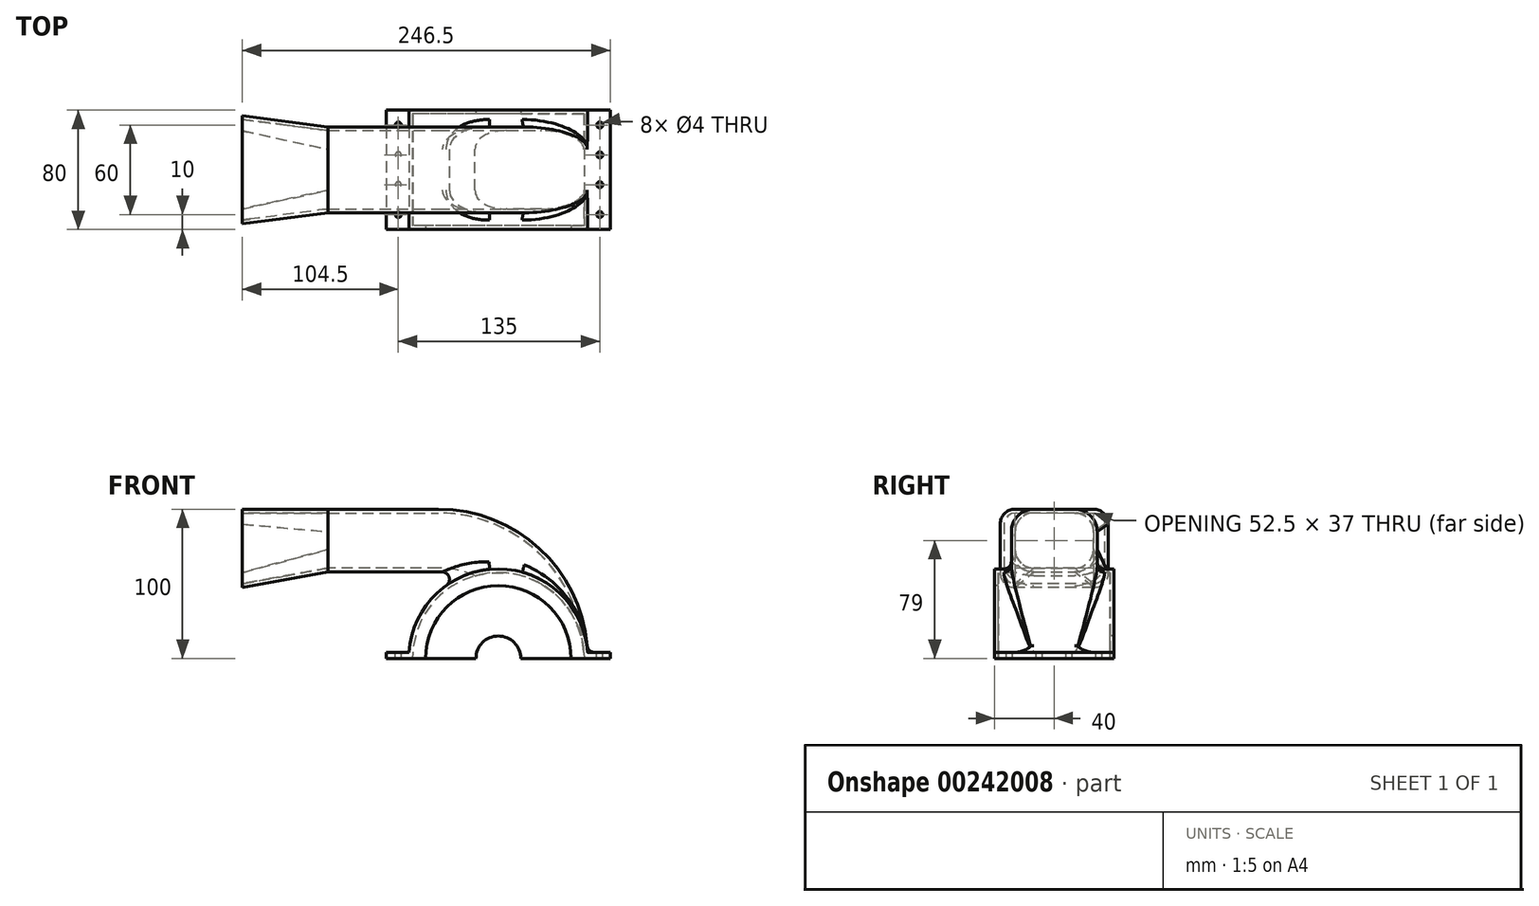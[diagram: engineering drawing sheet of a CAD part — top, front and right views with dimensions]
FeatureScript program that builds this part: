
annotation { "Feature Type Name" : "Feature", "Feature Type Description" : "" }
export const myFeature = defineFeature(function(context is Context, id is Id, definition is map)
    precondition{}
    {
        {
            var Q0;
            Q0=qCreatedBy(makeId("Front.planeOp"),FACE);
            var sketch = newSketch(context, id + "F0", { "sketchPlane" : qUnion([Q0])});
            skArc(sketch, "E0", {"start": v(15, 0) * mm, "mid": v(0, 15) * mm, "end": v(-15, 0) * mm});
            skArc(sketch, "E1", {"start": v(48.75, 0) * mm, "mid": v(0, 48.75) * mm, "end": v(-48.75, 0) * mm});
            skArc(sketch, "E2", {"start": v(59.87, 4) * mm, "mid": v(0, 60) * mm, "end": v(-59.87, 4) * mm});
            skLineSegment(sketch, "E3", {"start": v(15, 0) * mm, "end": v(75, 0) * mm});
            skLineSegment(sketch, "E4", {"start": v(-15, 0) * mm, "end": v(-75, 0) * mm});
            skLineSegment(sketch, "E5", {"start": v(75, 0) * mm, "end": v(75, 4) * mm});
            skLineSegment(sketch, "E6", {"start": v(75, 4) * mm, "end": v(59.87, 4) * mm});
            skLineSegment(sketch, "E7", {"start": v(-75, 0) * mm, "end": v(-75, 4) * mm});
            skLineSegment(sketch, "E8", {"start": v(-75, 4) * mm, "end": v(-59.87, 4) * mm});
            skPoint(sketch, "E9.orphan", {"position": v(-60, 0) * mm});
            skPoint(sketch, "E10.orphan", {"position": v(60, 0) * mm});
            skLineSegment(sketch, "E11", {"start": v(59.87, 4) * mm, "end": v(60, 0) * mm});
            skLineSegment(sketch, "E12", {"start": v(-59.87, 4) * mm, "end": v(-60, 0) * mm});
            skSolve(sketch);
        }
        {
            var Q0;
            {var subQ1=sQuery(id+"F0.wireOp",EDGE,"E1");Q0=makeQuery(id+"F0.imprint","IMPRINT",FACE,{"disambiguationData":[TD([[makeQuery(id+"F0.imprint","IMPRINT",EDGE,{"derivedFrom":subQ1}),-1.0]])]});}
            var Q1;
            {var subQ0=sQuery(id+"F0.wireOp",EDGE,"E0");Q1=makeQuery(id+"F0.imprint","IMPRINT",FACE,{"disambiguationData":[TD([[makeQuery(id+"F0.imprint","IMPRINT",EDGE,{"derivedFrom":subQ0}),-1.0]])]});}
            extrude(context, id + "F1", {"entities" : qUnion([Q0, Q1]), "oppositeDirection" : true, "depth" : 80 * mm});
        }
        {
            var Q0;
            Q0=qCreatedBy(makeId("Front.planeOp"),FACE);
            cPlane(context, id + "F2", {"entities" : qUnion([Q0]), "cplaneType" : CPlaneType.OFFSET, "offset" : 40 * mm, "oppositeDirection" : true, "width" : 150 * mm, "height" : 150 * mm});
        }
        {
            var Q0;
            Q0=qCreatedBy(id+"F2.planeOp",FACE);
            var sketch = newSketch(context, id + "F3", { "sketchPlane" : qUnion([Q0])});
            skArc(sketch, "E13.0", {"start": v(59.87, 4) * mm, "mid": v(0, 60) * mm, "end": v(-59.87, 4) * mm});
            skLineSegment(sketch, "E14", {"start": v(-114.05, 100) * mm, "end": v(-114.05, 58) * mm});
            skLineSegment(sketch, "E15", {"start": v(-114.05, 100) * mm, "end": v(-40.05, 100) * mm});
            skArc(sketch, "E16", {"start": v(-40.05, 100) * mm, "mid": v(29.23, 72.11) * mm, "end": v(59.87, 4) * mm});
            skLineSegment(sketch, "E17", {"start": v(-114.05, 58) * mm, "end": v(-15.36, 58) * mm});
            skLineSegment(sketch, "E18", {"start": v(-114.05, 100) * mm, "end": v(-171.55, 100) * mm});
            skLineSegment(sketch, "E19", {"start": v(-171.55, 100) * mm, "end": v(-171.55, 47.5) * mm});
            skLineSegment(sketch, "E20", {"start": v(-171.55, 47.5) * mm, "end": v(-114.05, 58) * mm});
            skSolve(sketch);
        }
        {
            var Q0;
            Q0=qCreatedBy(makeId("Right.planeOp"),FACE);
            cPlane(context, id + "F4", {"entities" : qUnion([Q0]), "cplaneType" : CPlaneType.OFFSET, "offset" : 114 * mm, "oppositeDirection" : true, "width" : 150 * mm, "height" : 150 * mm});
        }
        {
            var Q0;
            Q0=qCreatedBy(id+"F4.planeOp",FACE);
            var sketch = newSketch(context, id + "F5", { "sketchPlane" : qUnion([Q0])});
            skPoint(sketch, "E21", {"position": v(40, 79) * mm});
            skLineSegment(sketch, "E22.bottom", {"start": v(26.25, 100) * mm, "end": v(53.75, 100) * mm});
            skLineSegment(sketch, "E22.top", {"start": v(26.25, 58) * mm, "end": v(53.75, 58) * mm});
            skLineSegment(sketch, "E22.left", {"start": v(11.25, 85) * mm, "end": v(11.25, 73) * mm});
            skLineSegment(sketch, "E22.right", {"start": v(68.75, 85) * mm, "end": v(68.75, 73) * mm});
            skPoint(sketch, "E23.orphan", {"position": v(40, 100) * mm});
            skPoint(sketch, "E24.0.end.orphan", {"position": v(40, 58) * mm});
            skPoint(sketch, "E25.visualSharp", {"position": v(11.25, 100) * mm});
            skArc(sketch, "E25.filletArc", {"start": v(26.25, 100) * mm, "mid": v(15.64, 95.6) * mm, "end": v(11.25, 85) * mm});
            skPoint(sketch, "E26.visualSharp", {"position": v(11.25, 58) * mm});
            skArc(sketch, "E26.filletArc", {"start": v(11.25, 73) * mm, "mid": v(15.64, 62.4) * mm, "end": v(26.25, 58) * mm});
            skPoint(sketch, "E27.visualSharp", {"position": v(68.75, 58) * mm});
            skArc(sketch, "E27.filletArc", {"start": v(53.75, 58) * mm, "mid": v(64.36, 62.4) * mm, "end": v(68.75, 73) * mm});
            skPoint(sketch, "E28.visualSharp", {"position": v(68.75, 100) * mm});
            skArc(sketch, "E28.filletArc", {"start": v(68.75, 85) * mm, "mid": v(64.36, 95.6) * mm, "end": v(53.75, 100) * mm});
            skSolve(sketch);
        }
        {
            var Q0;
            Q0=makeQuery(id+"F5.imprint","IMPRINT",FACE,{"disambiguationData":[TD([[makeQuery(id+"F5.imprint","IMPRINT",EDGE,{"derivedFrom":sQuery(id+"F5.wireOp",EDGE,"E22.bottom")}),-1.0]])]});
            var Q1;
            Q1=sQuery(id+"F3.wireOp",EDGE,"E15");
            var Q2;
            Q2=sQuery(id+"F3.wireOp",EDGE,"E16");
            sweep(context, id + "F6", {"operationType" : NewBodyOperationType.ADD, "profiles" : qUnion([Q0]), "path" : qUnion([Q1, Q2])});
        }
        {
            var Q0;
            {var subQ0=sQuery(id+"F0.wireOp",EDGE,"E0");Q0=makeQuery(id+"F0.imprint","IMPRINT",FACE,{"disambiguationData":[TD([[makeQuery(id+"F0.imprint","IMPRINT",EDGE,{"derivedFrom":subQ0}),-1.0]])]});}
            extrude(context, id + "F7", {"entities" : qUnion([Q0]), "operationType" : NewBodyOperationType.REMOVE, "oppositeDirection" : true, "depth" : 77.5 * mm});
        }
        {
            var Q0;
            Q0=makeQuery(id+"F1.opExtrude","SWEPT_FACE",FACE,{"disambiguationData":[OSD([sQuery(id+"F0.wireOp",EDGE,"E3")])]});
            var Q1;
            Q1=makeQuery(id+"F7.boolean.opBoolean","COPY",FACE,{"derivedFrom":makeQuery(id+"F7.opExtrude","SWEPT_FACE",FACE,{"disambiguationData":[OSD([sQuery(id+"F0.wireOp",EDGE,"E1")])]})});
            var Q2;
            Q2=makeQuery(id+"F1.opExtrude","SWEPT_FACE",FACE,{"disambiguationData":[OSD([sQuery(id+"F0.wireOp",EDGE,"E4")])]});
            var Q3;
            Q3=makeQuery(id+"F6.opSweep","CAP_FACE",FACE,{"disambiguationData":[OSD([sQuery(id+"F3.wireOp",VERTEX,"E15.start"),sQuery(id+"F5.wireOp",EDGE,"E22.bottom"),sQuery(id+"F5.wireOp",EDGE,"E22.top"),sQuery(id+"F5.wireOp",EDGE,"E22.left"),sQuery(id+"F5.wireOp",EDGE,"E22.right"),sQuery(id+"F5.wireOp",EDGE,"E25.filletArc"),sQuery(id+"F5.wireOp",EDGE,"E26.filletArc"),sQuery(id+"F5.wireOp",EDGE,"E27.filletArc"),sQuery(id+"F5.wireOp",EDGE,"E28.filletArc")])],"isStart":true});
            var Q4;
            Q4=makeQuery(id+"F1.opExtrude","SWEPT_BODY",BODY,{"disambiguationData":[OSD([sQuery(id+"F0.wireOp",EDGE,"E0"),sQuery(id+"F0.wireOp",EDGE,"E2"),sQuery(id+"F0.wireOp",EDGE,"E3"),sQuery(id+"F0.wireOp",EDGE,"E4"),sQuery(id+"F0.wireOp",EDGE,"E5"),sQuery(id+"F0.wireOp",EDGE,"E6"),sQuery(id+"F0.wireOp",EDGE,"E7"),sQuery(id+"F0.wireOp",EDGE,"E8")])]});
            shell(context, id + "F8", {"entities" : qUnion([Q0, Q1, Q2, Q3]), "parts" : qUnion([Q4]), "thickness" : 2.5 * mm});
        }
        {
            var Q0;
            {var subQ0=sQuery(id+"F0.wireOp",EDGE,"E7");Q0=makeQuery(id+"F0.imprint","IMPRINT",FACE,{"disambiguationData":[TD([[makeQuery(id+"F0.imprint","IMPRINT",EDGE,{"derivedFrom":subQ0}),-1.0]])]});}
            var Q1;
            {var subQ0=sQuery(id+"F0.wireOp",EDGE,"E5");Q1=makeQuery(id+"F0.imprint","IMPRINT",FACE,{"disambiguationData":[TD([[makeQuery(id+"F0.imprint","IMPRINT",EDGE,{"derivedFrom":subQ0}),1.0]])]});}
            extrude(context, id + "F9", {"entities" : qUnion([Q0, Q1]), "operationType" : NewBodyOperationType.ADD, "oppositeDirection" : true, "depth" : 80 * mm});
        }
        {
            var Q0;
            Q0=makeQuery(id+"F9.opExtrude","SWEPT_FACE",FACE,{"disambiguationData":[OSD([sQuery(id+"F0.wireOp",EDGE,"E8")])]});
            var sketch = newSketch(context, id + "F10", { "sketchPlane" : qUnion([Q0])});
            skCircle(sketch, "E29", {"center": v(-67, 70) * mm, "radius": 2 * mm});
            skCircle(sketch, "E30.0.1.0", {"center": v(-67, 50) * mm, "radius": 2 * mm});
            skCircle(sketch, "E30.0.2.0", {"center": v(-67, 30) * mm, "radius": 2 * mm});
            skCircle(sketch, "E30.0.3.0", {"center": v(-67, 10) * mm, "radius": 2 * mm});
            skCircle(sketch, "E30.1.0.0", {"center": v(68, 70) * mm, "radius": 2 * mm});
            skCircle(sketch, "E30.1.1.0", {"center": v(68, 50) * mm, "radius": 2 * mm});
            skCircle(sketch, "E30.1.2.0", {"center": v(68, 30) * mm, "radius": 2 * mm});
            skCircle(sketch, "E30.1.3.0", {"center": v(68, 10) * mm, "radius": 2 * mm});
            skLineSegment(sketch, "E30.direction1", {"start": v(-67, 70) * mm, "end": v(68, 70) * mm, "construction": true});
            skLineSegment(sketch, "E30.direction2", {"start": v(-67, 70) * mm, "end": v(-67, 50) * mm, "construction": true});
            skSolve(sketch);
        }
        {
            var Q0;
            Q0 = qSketchRegion(id + "F10", true);
            extrude(context, id + "F11", {"entities" : qUnion([Q0]), "operationType" : NewBodyOperationType.REMOVE, "endBound" : BoundingType.THROUGH_ALL, "oppositeDirection" : true, "depth" : 25 * mm});
        }
        {
            var Q0;
            Q0=makeQuery(id+"F6.boolean.opBoolean","INTERSECT",EDGE,{"derivedFrom":[makeQuery(id+"F1.opExtrude","SWEPT_FACE",FACE,{"disambiguationData":[OSD([sQuery(id+"F0.wireOp",EDGE,"E2")])]}),makeQuery(id+"F6.opSweep","SWEPT_FACE",FACE,{"disambiguationData":[OSD([sQuery(id+"F3.wireOp",EDGE,"E16"),sQuery(id+"F5.wireOp",EDGE,"E22.top")])]})]});
            fillet(context, id + "F12", {"entities" : qUnion([Q0]), "radius" : 5 * mm, "tangentPropagation" : true, "allowEdgeOverflow" : false});
        }
        {
            var Q0;
            Q0=qCreatedBy(id+"F4.planeOp",FACE);
            cPlane(context, id + "F13", {"entities" : qUnion([Q0]), "cplaneType" : CPlaneType.OFFSET, "offset" : 57.5 * mm, "oppositeDirection" : true, "width" : 150 * mm, "height" : 150 * mm});
        }
        {
            var Q0;
            Q0=qCreatedBy(id+"F13.planeOp",FACE);
            var sketch = newSketch(context, id + "F14", { "sketchPlane" : qUnion([Q0])});
            skLineSegment(sketch, "E31.0", {"start": v(26.25, 100) * mm, "end": v(53.75, 100) * mm});
            skPoint(sketch, "E32", {"position": v(40, 100) * mm});
            skLineSegment(sketch, "E33.bottom", {"start": v(66.25, 100) * mm, "end": v(13.75, 100) * mm});
            skLineSegment(sketch, "E33.top", {"start": v(66.25, 47.5) * mm, "end": v(13.75, 47.5) * mm});
            skLineSegment(sketch, "E33.left", {"start": v(76.25, 90) * mm, "end": v(76.25, 57.5) * mm});
            skLineSegment(sketch, "E33.right", {"start": v(3.75, 90) * mm, "end": v(3.75, 57.5) * mm});
            skPoint(sketch, "E34.visualSharp", {"position": v(76.25, 100) * mm});
            skArc(sketch, "E34.filletArc", {"start": v(76.25, 90) * mm, "mid": v(73.32, 97.07) * mm, "end": v(66.25, 100) * mm});
            skPoint(sketch, "E35.visualSharp", {"position": v(76.25, 47.5) * mm});
            skArc(sketch, "E35.filletArc", {"start": v(66.25, 47.5) * mm, "mid": v(73.32, 50.43) * mm, "end": v(76.25, 57.5) * mm});
            skPoint(sketch, "E36.visualSharp", {"position": v(3.75, 100) * mm});
            skArc(sketch, "E36.filletArc", {"start": v(13.75, 100) * mm, "mid": v(6.68, 97.07) * mm, "end": v(3.75, 90) * mm});
            skPoint(sketch, "E37.visualSharp", {"position": v(3.75, 47.5) * mm});
            skArc(sketch, "E37.filletArc", {"start": v(3.75, 57.5) * mm, "mid": v(6.68, 50.43) * mm, "end": v(13.75, 47.5) * mm});
            skSolve(sketch);
        }
        {
            var Q1;
            Q1=makeQuery(id+"F14.imprint","IMPRINT",FACE,{"disambiguationData":[TD([[makeQuery(id+"F14.imprint","IMPRINT",EDGE,{"derivedFrom":sQuery(id+"F14.wireOp",EDGE,"E33.top")}),-1.0]])]});
            var Q2;
            Q2=makeQuery(id+"F5.imprint","IMPRINT",FACE,{"disambiguationData":[TD([[makeQuery(id+"F5.imprint","IMPRINT",EDGE,{"derivedFrom":sQuery(id+"F5.wireOp",EDGE,"E22.bottom")}),-1.0]])]});
            var Q3;
            Q3=sQuery(id+"F3.wireOp",EDGE,"E18");
            var Q4;
            Q4=sQuery(id+"F3.wireOp",EDGE,"E20");
            loft(context, id + "F15", {"sheetProfilesArray" : [{ "sheetProfileEntities" : qUnion([Q1]) }, { "sheetProfileEntities" : qUnion([Q2]) }], "guidesArray" : [{ "guideEntities" : qUnion([Q3]), "guideDerivativeType" : LoftGuideDerivativeType.DEFAULT, "guideDerivativeMagnitude" : 1 }, { "guideEntities" : qUnion([Q4]), "guideDerivativeType" : LoftGuideDerivativeType.DEFAULT, "guideDerivativeMagnitude" : 1 }]});
        }
        {
            var Q0;
            Q0=makeQuery(id+"F15.opLoft","CAP_FACE",FACE,{"disambiguationData":[OSD([makeQuery(id+"F14.imprint","IMPRINT",FACE,{"disambiguationData":[TD([[makeQuery(id+"F14.imprint","IMPRINT",EDGE,{"derivedFrom":sQuery(id+"F14.wireOp",EDGE,"E33.top")}),-1.0]])]})])],"isStart":true});
            var Q1;
            Q1=makeQuery(id+"F15.opLoft","CAP_FACE",FACE,{"disambiguationData":[OSD([makeQuery(id+"F5.imprint","IMPRINT",FACE,{"disambiguationData":[TD([[makeQuery(id+"F5.imprint","IMPRINT",EDGE,{"derivedFrom":sQuery(id+"F5.wireOp",EDGE,"E22.bottom")}),-1.0]])]})])],"isStart":true});
            shell(context, id + "F16", {"entities" : qUnion([Q0, Q1]), "thickness" : 2.5 * mm});
        }
    });
